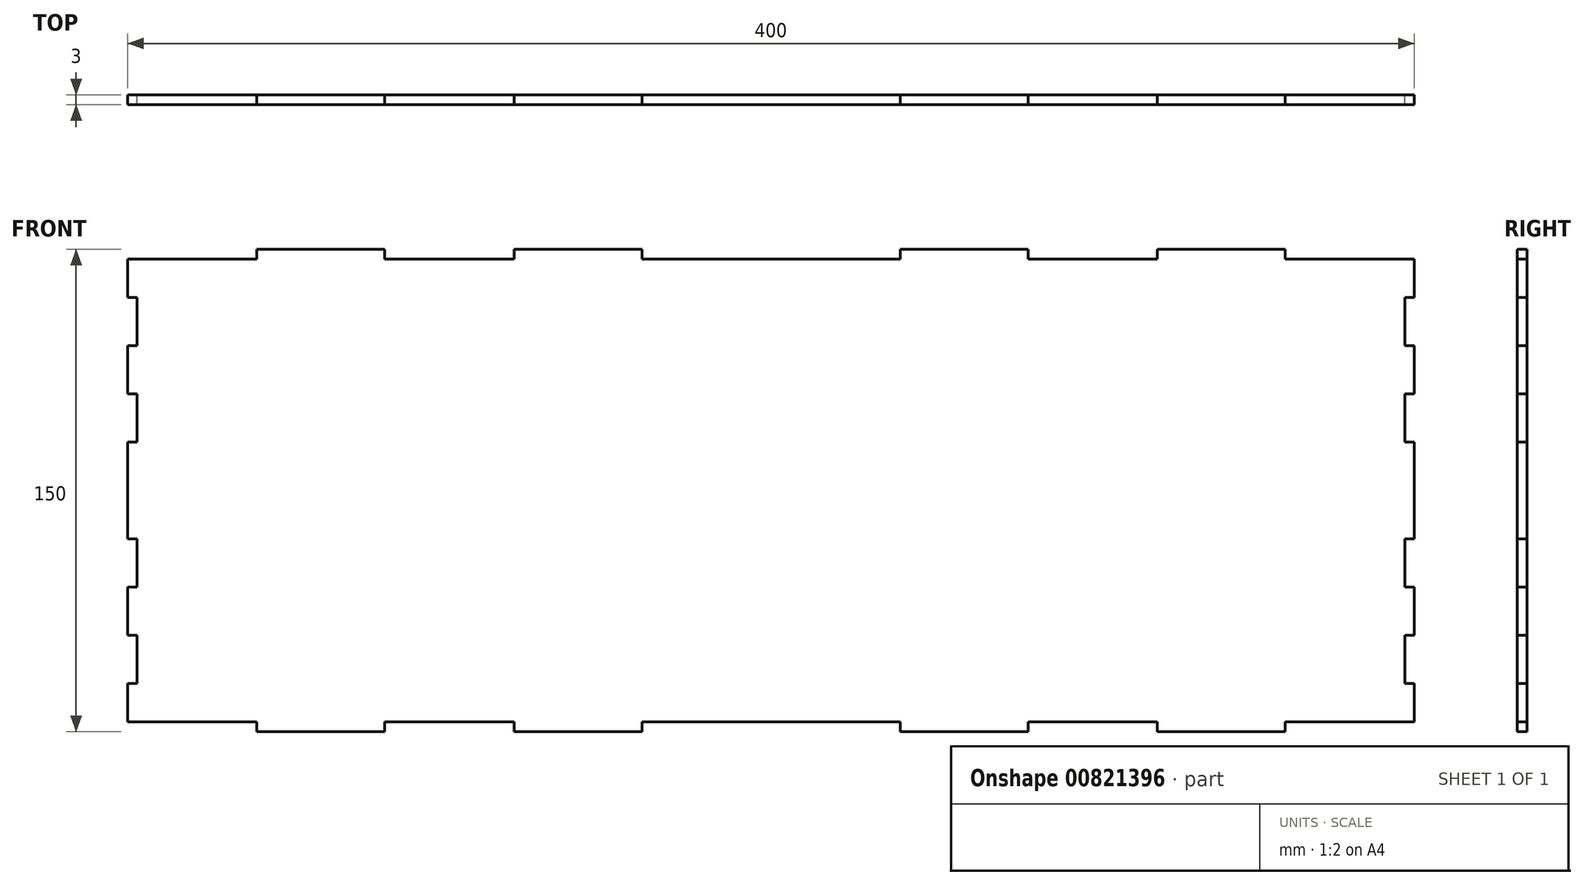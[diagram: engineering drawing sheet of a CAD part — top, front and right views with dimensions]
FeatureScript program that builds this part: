
annotation { "Feature Type Name" : "Feature", "Feature Type Description" : "" }
export const myFeature = defineFeature(function(context is Context, id is Id, definition is map)
    precondition{}
    {
        {
            var Q0;
            Q0=qCreatedBy(makeId("Front.planeOp"),FACE);
            var sketch = newSketch(context, id + "F0", { "sketchPlane" : qUnion([Q0])});
            skPoint(sketch, "E0.middle", {"position": v(0, 0) * mm});
            skLineSegment(sketch, "E1", {"start": v(-159.88, -75) * mm, "end": v(-159.88, -72) * mm});
            skLineSegment(sketch, "E2", {"start": v(-120.13, -72) * mm, "end": v(-120.13, -75) * mm});
            skLineSegment(sketch, "E3", {"start": v(-79.88, -75) * mm, "end": v(-79.88, -72) * mm});
            skLineSegment(sketch, "E4", {"start": v(-40.13, -72) * mm, "end": v(-40.13, -75) * mm});
            skLineSegment(sketch, "E5.MirrorCS", {"start": v(40.13, -72) * mm, "end": v(40.13, -75) * mm});
            skLineSegment(sketch, "E6", {"start": v(-159.88, -72) * mm, "end": v(-200, -72) * mm});
            skLineSegment(sketch, "E7", {"start": v(-159.88, -75) * mm, "end": v(-120.13, -75) * mm});
            skLineSegment(sketch, "E8", {"start": v(-120.13, -72) * mm, "end": v(-79.88, -72) * mm});
            skLineSegment(sketch, "E9", {"start": v(-79.88, -75) * mm, "end": v(-40.13, -75) * mm});
            skLineSegment(sketch, "E10", {"start": v(-40.13, -72) * mm, "end": v(40.13, -72) * mm});
            skLineSegment(sketch, "E11.MirrorCS", {"start": v(79.88, -75) * mm, "end": v(79.88, -72) * mm});
            skLineSegment(sketch, "E12.MirrorCS", {"start": v(159.88, -75) * mm, "end": v(159.88, -72) * mm});
            skLineSegment(sketch, "E13.MirrorCS", {"start": v(120.13, -72) * mm, "end": v(120.13, -75) * mm});
            skLineSegment(sketch, "E14.MirrorCS", {"start": v(120.13, -72) * mm, "end": v(79.88, -72) * mm});
            skLineSegment(sketch, "E15.MirrorCS", {"start": v(159.88, -75) * mm, "end": v(120.13, -75) * mm});
            skLineSegment(sketch, "E16.MirrorCS", {"start": v(159.88, -72) * mm, "end": v(200, -72) * mm});
            skLineSegment(sketch, "E17.MirrorCS", {"start": v(79.88, -75) * mm, "end": v(40.13, -75) * mm});
            skLineSegment(sketch, "E18.MirrorCS", {"start": v(159.88, 75) * mm, "end": v(159.88, 72) * mm});
            skLineSegment(sketch, "E19.MirrorCS", {"start": v(-79.88, 75) * mm, "end": v(-79.88, 72) * mm});
            skLineSegment(sketch, "E20.MirrorCS", {"start": v(-120.13, 72) * mm, "end": v(-120.13, 75) * mm});
            skLineSegment(sketch, "E21.MirrorCS", {"start": v(120.13, 72) * mm, "end": v(120.13, 75) * mm});
            skLineSegment(sketch, "E22.MirrorCS", {"start": v(40.13, 72) * mm, "end": v(40.13, 75) * mm});
            skLineSegment(sketch, "E23.MirrorCS", {"start": v(-40.13, 72) * mm, "end": v(-40.13, 75) * mm});
            skLineSegment(sketch, "E24.MirrorCS", {"start": v(-159.88, 75) * mm, "end": v(-159.88, 72) * mm});
            skLineSegment(sketch, "E25.MirrorCS", {"start": v(79.88, 75) * mm, "end": v(79.88, 72) * mm});
            skLineSegment(sketch, "E26.MirrorCS", {"start": v(-79.88, 75) * mm, "end": v(-40.13, 75) * mm});
            skLineSegment(sketch, "E27.MirrorCS", {"start": v(159.88, 72) * mm, "end": v(200, 72) * mm});
            skLineSegment(sketch, "E28.MirrorCS", {"start": v(-159.88, 72) * mm, "end": v(-200, 72) * mm});
            skLineSegment(sketch, "E29.MirrorCS", {"start": v(-159.88, 75) * mm, "end": v(-120.13, 75) * mm});
            skLineSegment(sketch, "E30.MirrorCS", {"start": v(79.88, 75) * mm, "end": v(40.13, 75) * mm});
            skLineSegment(sketch, "E31.MirrorCS", {"start": v(-40.13, 72) * mm, "end": v(40.13, 72) * mm});
            skLineSegment(sketch, "E32.MirrorCS", {"start": v(-120.13, 72) * mm, "end": v(-79.88, 72) * mm});
            skLineSegment(sketch, "E33.MirrorCS", {"start": v(120.13, 72) * mm, "end": v(79.88, 72) * mm});
            skLineSegment(sketch, "E34.MirrorCS", {"start": v(159.88, 75) * mm, "end": v(120.13, 75) * mm});
            skLineSegment(sketch, "E35", {"start": v(200, -72) * mm, "end": v(200, -60) * mm});
            skLineSegment(sketch, "E36", {"start": v(200, -60) * mm, "end": v(197, -60) * mm});
            skLineSegment(sketch, "E37", {"start": v(197, -60) * mm, "end": v(197, -45) * mm});
            skLineSegment(sketch, "E38", {"start": v(197, -45) * mm, "end": v(200, -45) * mm});
            skLineSegment(sketch, "E39", {"start": v(200, -45) * mm, "end": v(200, -30) * mm});
            skLineSegment(sketch, "E40", {"start": v(200, -30) * mm, "end": v(197, -30) * mm});
            skLineSegment(sketch, "E41", {"start": v(197, -30) * mm, "end": v(197, -15) * mm});
            skLineSegment(sketch, "E42", {"start": v(197, -15) * mm, "end": v(200, -15) * mm});
            skLineSegment(sketch, "E43.MirrorCS", {"start": v(197, 15) * mm, "end": v(200, 15) * mm});
            skLineSegment(sketch, "E44.MirrorCS", {"start": v(200, 30) * mm, "end": v(197, 30) * mm});
            skLineSegment(sketch, "E45.MirrorCS", {"start": v(197, 45) * mm, "end": v(200, 45) * mm});
            skLineSegment(sketch, "E46.MirrorCS", {"start": v(200, 60) * mm, "end": v(197, 60) * mm});
            skLineSegment(sketch, "E47.MirrorCS", {"start": v(197, 60) * mm, "end": v(197, 45) * mm});
            skLineSegment(sketch, "E48.MirrorCS", {"start": v(197, 30) * mm, "end": v(197, 15) * mm});
            skLineSegment(sketch, "E49.MirrorCS", {"start": v(200, 45) * mm, "end": v(200, 30) * mm});
            skLineSegment(sketch, "E50.MirrorCS", {"start": v(200, 72) * mm, "end": v(200, 60) * mm});
            skLineSegment(sketch, "E51", {"start": v(200, -15) * mm, "end": v(200, 15) * mm});
            skLineSegment(sketch, "E52.MirrorCS", {"start": v(-197, -15) * mm, "end": v(-200, -15) * mm});
            skLineSegment(sketch, "E53.MirrorCS", {"start": v(-200, 60) * mm, "end": v(-197, 60) * mm});
            skLineSegment(sketch, "E54.MirrorCS", {"start": v(-200, -30) * mm, "end": v(-197, -30) * mm});
            skLineSegment(sketch, "E55.MirrorCS", {"start": v(-200, 30) * mm, "end": v(-197, 30) * mm});
            skLineSegment(sketch, "E56.MirrorCS", {"start": v(-197, 15) * mm, "end": v(-200, 15) * mm});
            skLineSegment(sketch, "E57.MirrorCS", {"start": v(-197, -45) * mm, "end": v(-200, -45) * mm});
            skLineSegment(sketch, "E58.MirrorCS", {"start": v(-200, -60) * mm, "end": v(-197, -60) * mm});
            skLineSegment(sketch, "E59.MirrorCS", {"start": v(-197, 45) * mm, "end": v(-200, 45) * mm});
            skLineSegment(sketch, "E60.MirrorCS", {"start": v(-197, 60) * mm, "end": v(-197, 45) * mm});
            skLineSegment(sketch, "E61.MirrorCS", {"start": v(-200, -15) * mm, "end": v(-200, 15) * mm});
            skLineSegment(sketch, "E62.MirrorCS", {"start": v(-200, 45) * mm, "end": v(-200, 30) * mm});
            skLineSegment(sketch, "E63.MirrorCS", {"start": v(-200, -72) * mm, "end": v(-200, -60) * mm});
            skLineSegment(sketch, "E64.MirrorCS", {"start": v(-197, -60) * mm, "end": v(-197, -45) * mm});
            skLineSegment(sketch, "E65.MirrorCS", {"start": v(-197, -30) * mm, "end": v(-197, -15) * mm});
            skLineSegment(sketch, "E66.MirrorCS", {"start": v(-200, -45) * mm, "end": v(-200, -30) * mm});
            skLineSegment(sketch, "E67.MirrorCS", {"start": v(-200, 72) * mm, "end": v(-200, 60) * mm});
            skLineSegment(sketch, "E68.MirrorCS", {"start": v(-197, 30) * mm, "end": v(-197, 15) * mm});
            skSolve(sketch);
        }
        {
            var Q0;
            Q0=makeQuery(id+"F0.imprint","IMPRINT",FACE,{"disambiguationData":[TD([[makeQuery(id+"F0.imprint","IMPRINT",EDGE,{"derivedFrom":sQuery(id+"F0.wireOp",EDGE,"E1")}),-1.0]])]});
            extrude(context, id + "F1", {"entities" : qUnion([Q0]), "depth" : 3 * mm, "offsetDistance" : 25 * mm});
        }
    });
